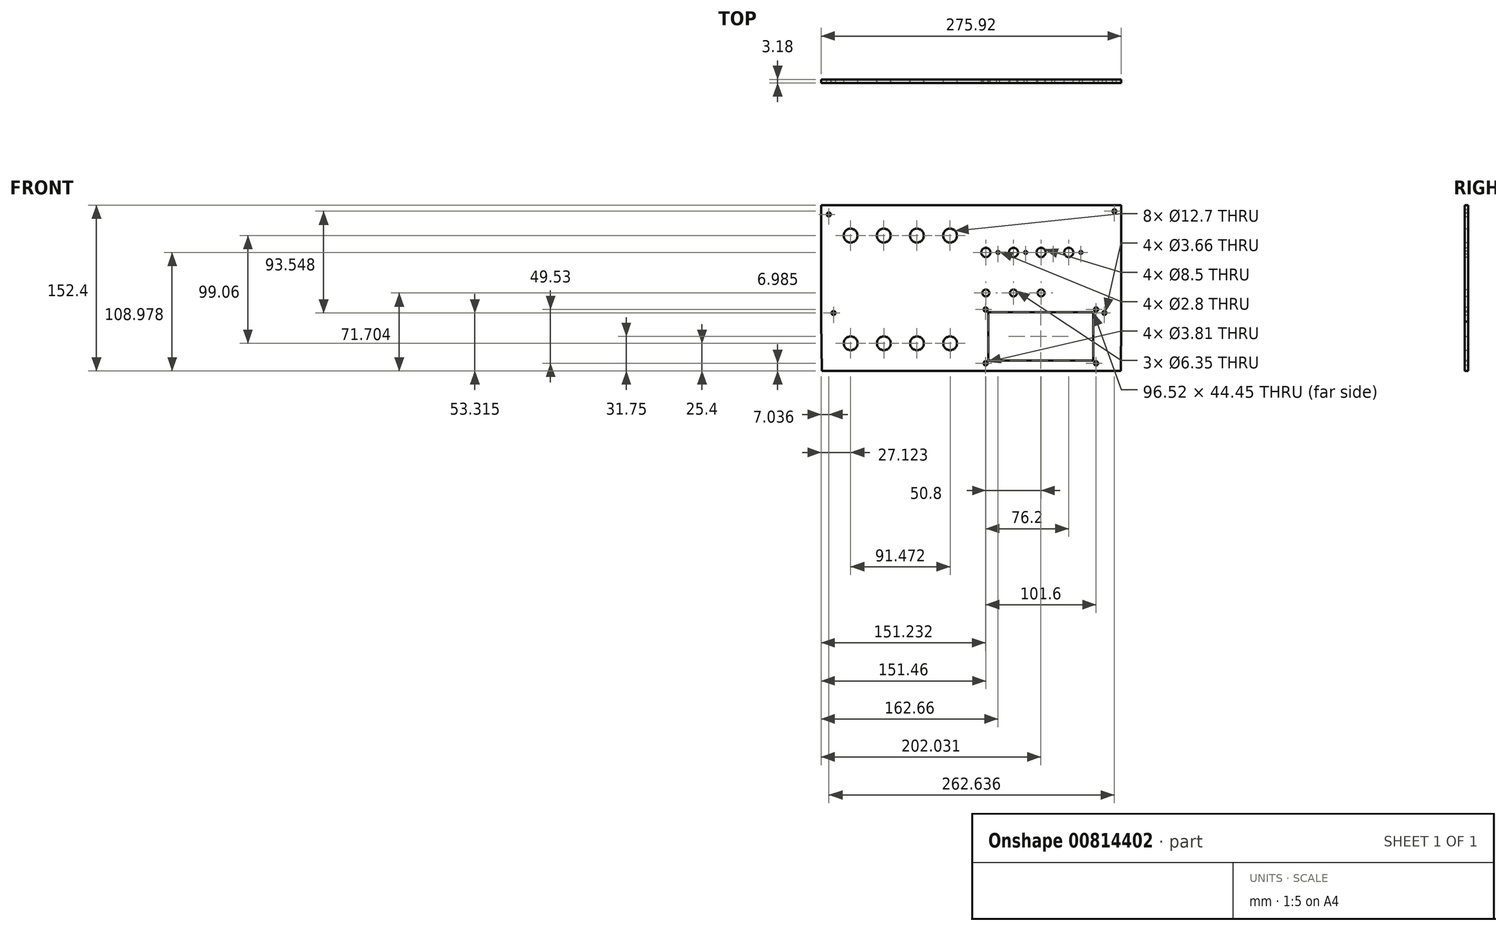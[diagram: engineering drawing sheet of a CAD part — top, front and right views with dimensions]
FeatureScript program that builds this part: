
annotation { "Feature Type Name" : "Feature", "Feature Type Description" : "" }
export const myFeature = defineFeature(function(context is Context, id is Id, definition is map)
    precondition{}
    {
        {
            var Q0;
            Q0=qCreatedBy(makeId("Front.planeOp"),FACE);
            var sketch = newSketch(context, id + "F0", { "sketchPlane" : qUnion([Q0])});
            skCircle(sketch, "E0", {"center": v(-130.92, 67.7) * mm, "radius": 1.83 * mm});
            skCircle(sketch, "E1", {"center": v(-126.58, -22.89) * mm, "radius": 1.83 * mm});
            skCircle(sketch, "E2", {"center": v(122.5, -22.89) * mm, "radius": 1.83 * mm});
            skCircle(sketch, "E3", {"center": v(131.71, 70.66) * mm, "radius": 1.83 * mm});
            skCircle(sketch, "E4", {"center": v(-19.36, -50.8) * mm, "radius": 6.35 * mm});
            skCircle(sketch, "E5", {"center": v(-49.88, 48.26) * mm, "radius": 6.35 * mm});
            skCircle(sketch, "E6", {"center": v(-49.84, -50.8) * mm, "radius": 6.35 * mm});
            skCircle(sketch, "E7", {"center": v(-80.36, 48.26) * mm, "radius": 6.35 * mm});
            skCircle(sketch, "E8", {"center": v(-110.8, -50.8) * mm, "radius": 6.35 * mm});
            skCircle(sketch, "E9", {"center": v(13.5, 32.78) * mm, "radius": 4.25 * mm});
            skCircle(sketch, "E10", {"center": v(24.7, 32.78) * mm, "radius": 1.4 * mm});
            skCircle(sketch, "E11", {"center": v(13.5, -4.5) * mm, "radius": 3.18 * mm});
            skCircle(sketch, "E12", {"center": v(38.9, -4.5) * mm, "radius": 3.18 * mm});
            skCircle(sketch, "E13", {"center": v(38.9, 32.78) * mm, "radius": 4.25 * mm});
            skCircle(sketch, "E14", {"center": v(50.1, 32.78) * mm, "radius": 1.4 * mm});
            skCircle(sketch, "E15", {"center": v(64.3, 32.78) * mm, "radius": 4.25 * mm});
            skCircle(sketch, "E16", {"center": v(75.5, 32.78) * mm, "radius": 1.4 * mm});
            skCircle(sketch, "E17", {"center": v(89.7, 32.78) * mm, "radius": 4.25 * mm});
            skCircle(sketch, "E18", {"center": v(100.9, 32.78) * mm, "radius": 1.4 * mm});
            skCircle(sketch, "E19", {"center": v(-80.32, -50.8) * mm, "radius": 6.35 * mm});
            skLineSegment(sketch, "E20", {"start": v(-137.96, 76.2) * mm, "end": v(-137.95, 37.39) * mm});
            skLineSegment(sketch, "E21", {"start": v(137.83, 76.2) * mm, "end": v(-137.96, 76.2) * mm});
            skLineSegment(sketch, "E22", {"start": v(137.82, 36.96) * mm, "end": v(137.83, 76.2) * mm});
            skLineSegment(sketch, "E23", {"start": v(137.96, -9) * mm, "end": v(137.82, 36.96) * mm});
            skLineSegment(sketch, "E24", {"start": v(137.96, -30.91) * mm, "end": v(137.96, -9) * mm});
            skLineSegment(sketch, "E25", {"start": v(137.5, -76.2) * mm, "end": v(137.96, -30.91) * mm});
            skLineSegment(sketch, "E26", {"start": v(-137.48, -76.2) * mm, "end": v(137.5, -76.2) * mm});
            skLineSegment(sketch, "E27", {"start": v(-137.93, -30.91) * mm, "end": v(-137.48, -76.2) * mm});
            skLineSegment(sketch, "E28", {"start": v(-137.93, -9) * mm, "end": v(-137.93, -30.91) * mm});
            skLineSegment(sketch, "E29", {"start": v(-137.95, 37.39) * mm, "end": v(-137.93, -9) * mm});
            skSolve(sketch);
        }
        {
            var Q0;
            Q0 = qSketchRegion(id + "F0", true);
            extrude(context, id + "F1", {"entities" : qUnion([Q0]), "depth" : 3.17 * mm, "offsetDistance" : 25.4 * mm});
        }
        {
            var Q0;
            Q0=makeQuery(id+"F1.opExtrude","CAP_FACE",FACE,{"disambiguationData":[OSD([sQuery(id+"F0.wireOp",EDGE,"E4"),sQuery(id+"F0.wireOp",EDGE,"E5"),sQuery(id+"F0.wireOp",EDGE,"E6"),sQuery(id+"F0.wireOp",EDGE,"E7"),sQuery(id+"F0.wireOp",EDGE,"E3"),sQuery(id+"F0.wireOp",EDGE,"E1"),sQuery(id+"F0.wireOp",EDGE,"E0"),sQuery(id+"F0.wireOp",EDGE,"E2"),sQuery(id+"F0.wireOp",EDGE,"E8"),sQuery(id+"F0.wireOp",EDGE,"E9"),sQuery(id+"F0.wireOp",EDGE,"E10"),sQuery(id+"F0.wireOp",EDGE,"E11"),sQuery(id+"F0.wireOp",EDGE,"E12"),sQuery(id+"F0.wireOp",EDGE,"E13"),sQuery(id+"F0.wireOp",EDGE,"E14"),sQuery(id+"F0.wireOp",EDGE,"E15"),sQuery(id+"F0.wireOp",EDGE,"E16"),sQuery(id+"F0.wireOp",EDGE,"eac8aa70-fe84-43e1-8b47-51b2e9a8b7fa"),sQuery(id+"F0.wireOp",EDGE,"b448d256-9c96-460c-9653-0981c481f15a"),sQuery(id+"F0.wireOp",EDGE,"E17"),sQuery(id+"F0.wireOp",EDGE,"E18"),sQuery(id+"F0.wireOp",EDGE,"5e0640d2-4cce-4d1b-b867-bfe2c8a8024b"),sQuery(id+"F0.wireOp",EDGE,"7c8e2c1e-26ed-46b7-8e98-9c29e88a8567"),sQuery(id+"F0.wireOp",EDGE,"E19"),sQuery(id+"F0.wireOp",EDGE,"E20"),sQuery(id+"F0.wireOp",EDGE,"E21"),sQuery(id+"F0.wireOp",EDGE,"E22"),sQuery(id+"F0.wireOp",EDGE,"E23"),sQuery(id+"F0.wireOp",EDGE,"E24"),sQuery(id+"F0.wireOp",EDGE,"E25"),sQuery(id+"F0.wireOp",EDGE,"E26"),sQuery(id+"F0.wireOp",EDGE,"E27"),sQuery(id+"F0.wireOp",EDGE,"E28"),sQuery(id+"F0.wireOp",EDGE,"E29")])],"isStart":false});
            var sketch = newSketch(context, id + "F2", { "sketchPlane" : qUnion([Q0])});
            skCircle(sketch, "E30", {"center": v(-110.84, 48.26) * mm, "radius": 6.35 * mm});
            skCircle(sketch, "E31", {"center": v(-19.4, 48.26) * mm, "radius": 6.35 * mm});
            skCircle(sketch, "E32", {"center": v(64.3, -4.5) * mm, "radius": 3.18 * mm});
            skLineSegment(sketch, "E33.bottom", {"start": v(15.81, -22.22) * mm, "end": v(112.33, -22.22) * mm});
            skLineSegment(sketch, "E33.top", {"start": v(15.81, -66.67) * mm, "end": v(112.33, -66.67) * mm});
            skLineSegment(sketch, "E33.left", {"start": v(15.81, -22.22) * mm, "end": v(15.81, -66.67) * mm});
            skLineSegment(sketch, "E33.right", {"start": v(112.33, -22.22) * mm, "end": v(112.33, -66.67) * mm});
            skCircle(sketch, "E34", {"center": v(13.27, -69.22) * mm, "radius": 1.9 * mm});
            skCircle(sketch, "E35.0.1.0", {"center": v(13.27, -19.68) * mm, "radius": 1.9 * mm});
            skCircle(sketch, "E35.1.0.0", {"center": v(114.87, -69.22) * mm, "radius": 1.9 * mm});
            skCircle(sketch, "E35.1.1.0", {"center": v(114.87, -19.68) * mm, "radius": 1.9 * mm});
            skLineSegment(sketch, "E35.direction1", {"start": v(13.27, -69.22) * mm, "end": v(114.87, -69.22) * mm, "construction": true});
            skLineSegment(sketch, "E35.direction2", {"start": v(13.27, -69.22) * mm, "end": v(13.27, -19.68) * mm, "construction": true});
            skSolve(sketch);
        }
        {
            var Q0;
            Q0 = qSketchRegion(id + "F2", true);
            extrude(context, id + "F3", {"entities" : qUnion([Q0]), "operationType" : NewBodyOperationType.REMOVE, "oppositeDirection" : true, "depth" : 25.4 * mm, "offsetDistance" : 25.4 * mm});
        }
    });
